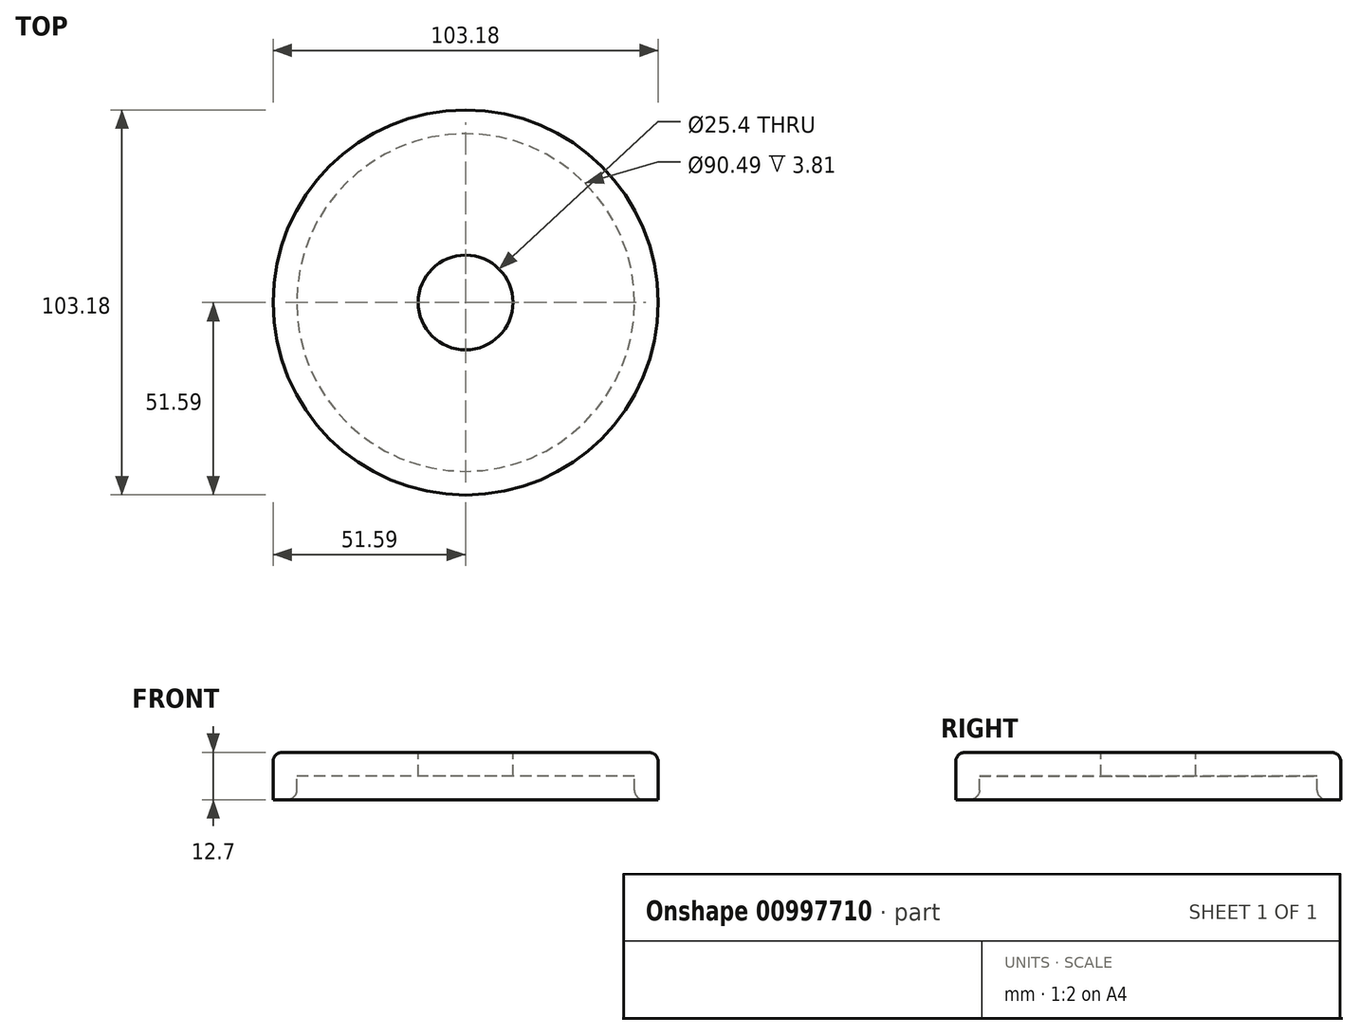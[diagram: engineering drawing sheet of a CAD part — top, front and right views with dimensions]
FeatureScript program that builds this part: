
annotation { "Feature Type Name" : "Feature", "Feature Type Description" : "" }
export const myFeature = defineFeature(function(context is Context, id is Id, definition is map)
    precondition{}
    {
        {
            var Q0;
            Q0=qCreatedBy(makeId("Top.planeOp"),FACE);
            var sketch = newSketch(context, id + "F0", { "sketchPlane" : qUnion([Q0])});
            skCircle(sketch, "E0", {"center": v(0, 0) * mm, "radius": 45.24 * mm});
            skCircle(sketch, "E1", {"center": v(0, 0) * mm, "radius": 12.7 * mm});
            skCircle(sketch, "E2.0", {"center": v(0, 0) * mm, "radius": 51.6 * mm});
            skSolve(sketch);
        }
        {
            var Q0;
            Q0=makeQuery(id+"F0.imprint","IMPRINT",FACE,{"disambiguationData":[TD([[makeQuery(id+"F0.imprint","IMPRINT",EDGE,{"derivedFrom":sQuery(id+"F0.wireOp",EDGE,"E0")}),1.0]])]});
            extrude(context, id + "F1", {"entities" : qUnion([Q0]), "oppositeDirection" : true, "depth" : 6.35 * mm, "offsetDistance" : 25.4 * mm});
        }
        {
            var Q0;
            Q0=makeQuery(id+"F0.imprint","IMPRINT",FACE,{"disambiguationData":[TD([[makeQuery(id+"F0.imprint","IMPRINT",EDGE,{"derivedFrom":sQuery(id+"F0.wireOp",EDGE,"E0")}),-1.0]])]});
            extrude(context, id + "F2", {"entities" : qUnion([Q0]), "operationType" : NewBodyOperationType.ADD, "oppositeDirection" : true, "depth" : 12.7 * mm, "offsetDistance" : 25.4 * mm});
        }
        {
            var Q0;
            Q0=makeQuery(id+"F2.opExtrude","CAP_EDGE",EDGE,{"disambiguationData":[OSD([sQuery(id+"F0.wireOp",EDGE,"E2.0")])],"isStart":true});
            fillet(context, id + "F3", {"entities" : qUnion([Q0]), "radius" : 2.54 * mm, "tangentPropagation" : true, "allowEdgeOverflow" : false});
        }
        {
            var Q0;
            Q0=makeQuery(id+"F2.opExtrude","CAP_EDGE",EDGE,{"disambiguationData":[OSD([sQuery(id+"F0.wireOp",EDGE,"E0")])],"isStart":false});
            fillet(context, id + "F4", {"entities" : qUnion([Q0]), "radius" : 2.54 * mm, "tangentPropagation" : true, "allowEdgeOverflow" : false});
        }
    });
